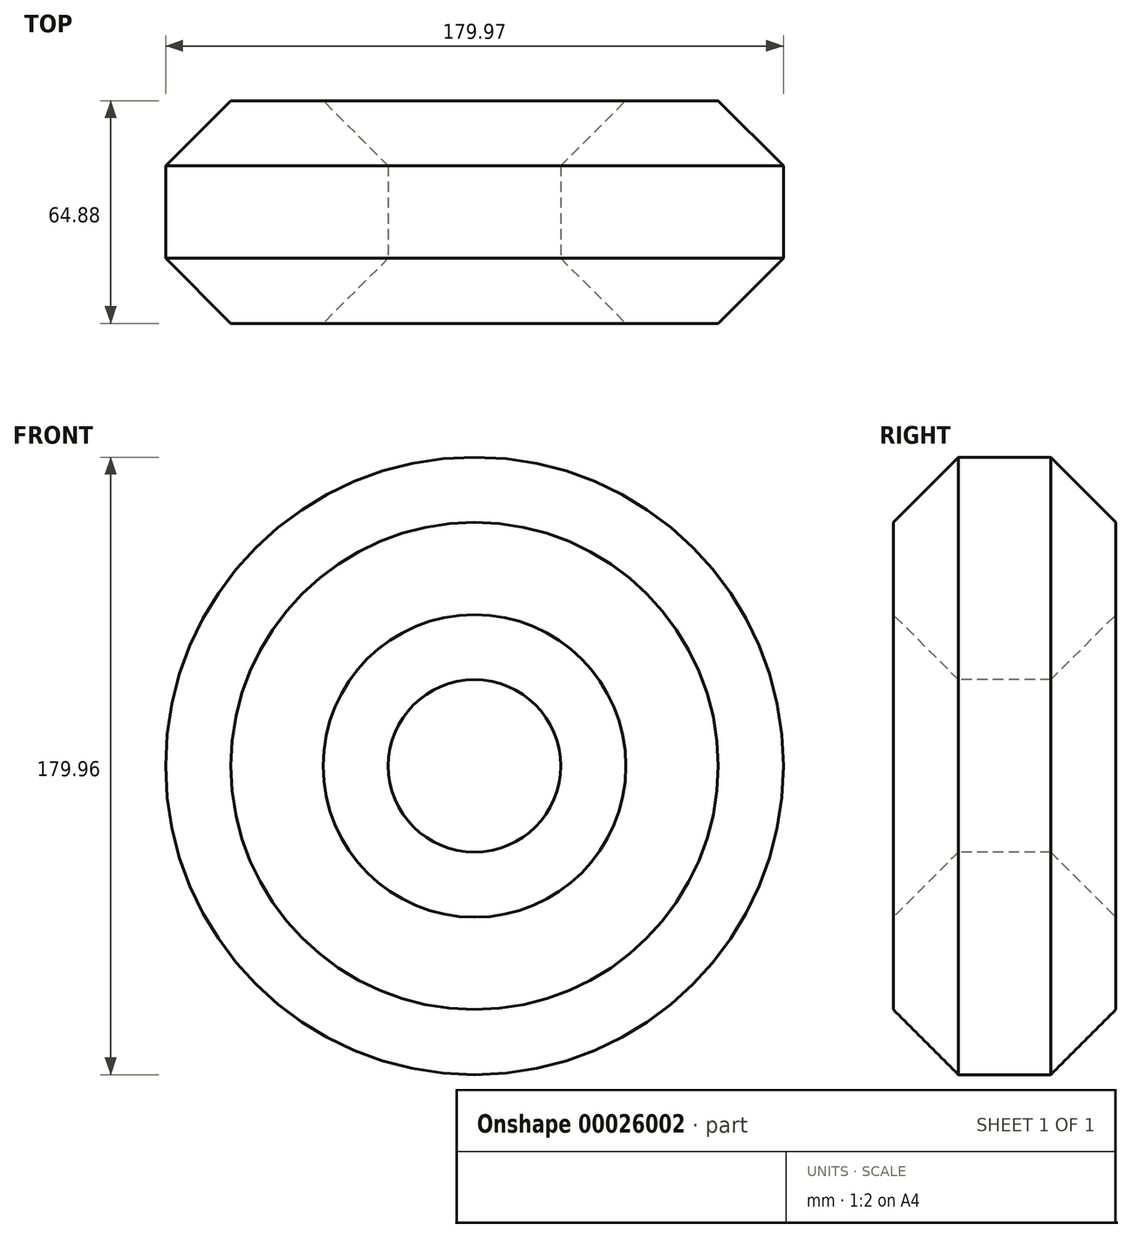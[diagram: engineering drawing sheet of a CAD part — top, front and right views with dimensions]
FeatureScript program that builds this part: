
annotation { "Feature Type Name" : "Feature", "Feature Type Description" : "" }
export const myFeature = defineFeature(function(context is Context, id is Id, definition is map)
    precondition{}
    {
        {
            var Q0;
            Q0=qCreatedBy(makeId("Top.planeOp"),FACE);
            var sketch = newSketch(context, id + "F0", { "sketchPlane" : qUnion([Q0])});
            skCircle(sketch, "E0.cCircle", {"center": v(13.26, 0) * mm, "radius": 32.44 * mm, "construction": true});
            skLineSegment(sketch, "E0.0", {"start": v(45.7, 13.44) * mm, "end": v(45.7, -13.44) * mm});
            skLineSegment(sketch, "E0.1", {"start": v(45.7, -13.44) * mm, "end": v(26.7, -32.44) * mm});
            skLineSegment(sketch, "E0.2", {"start": v(26.7, -32.44) * mm, "end": v(-0.18, -32.44) * mm});
            skLineSegment(sketch, "E0.3", {"start": v(-0.18, -32.44) * mm, "end": v(-19.18, -13.44) * mm});
            skLineSegment(sketch, "E0.4", {"start": v(-19.18, -13.44) * mm, "end": v(-19.18, 13.44) * mm});
            skLineSegment(sketch, "E0.5", {"start": v(-19.18, 13.44) * mm, "end": v(-0.18, 32.44) * mm});
            skLineSegment(sketch, "E0.6", {"start": v(-0.18, 32.44) * mm, "end": v(26.7, 32.44) * mm});
            skLineSegment(sketch, "E0.7", {"start": v(26.7, 32.44) * mm, "end": v(45.7, 13.44) * mm});
            skPoint(sketch, "E0.0.midPoint", {"position": v(45.7, 0) * mm});
            skLineSegment(sketch, "E1", {"start": v(-44.28, -70.17) * mm, "end": v(-44.28, 69.98) * mm});
            skSolve(sketch);
        }
        {
            var Q0;
            Q0 = qSketchRegion(id + "F0", true);
            var Q1;
            Q1=sQuery(id+"F0.wireOp",EDGE,"E1");
            revolve(context, id + "F1", {"entities" : qUnion([Q0]), "axis" : qUnion([Q1]), "revolveType" : RevolveType.FULL});
        }
    });
